# Revit family: HEATER MIX
name_source: partatom
category: Wyposażenie mechaniczne
revit_build: Autodesk Revit 2018 (Build: 20170927_1515(x64)
units: mm (PartAtom-declared; Revit-internal decimal feet)

## family parameters
Klasyfikacja = Brak
Obiekt nadrzędny = Powierzchnia
Punkt obliczania pomieszczeń = Nie
Tnij formami wycięć po wczytaniu = Nie
Typ części = Normalny
Współdzielony = Nie
Wymiar okrągłego złącza = Użyj średnicy

## types (1)
- HEATER MIX
    Autor = www.archispace.com
    Domyślna rzędna = 1219 mm
    Model = Mix
    Opis = Nagrzewnica Heater MIX
    Producent = SONNIGER Polska Sp. z o.o. Sp. k.
    głośność pracy (dB) = 60.5
    klasa IP = IP54
    maksymalny wydatek powietrza = 5600.0 m³/h
    materiał = 230,230,230
    moc silnika elektrycznego = 360 W
    napięcie zasilania = 230 V
    obroty silnika (obr/min) = 1400
    pole pracy max. = 380 m²
    pole pracy min. = 200 m²
    waga bez wody = 9.20 kg
    waga z wodą = 9.20 kg
    wysokość montażu max. = 15 mm
    wysokość montażu min. = 9 mm
